annotation { "Feature Type Name" : "Feature", "Feature Type Description" : "" }
export const myFeature = defineFeature(function(context is Context, id is Id, definition is map)
    precondition{}
    {
        {
            var Q0;
            Q0=qCreatedBy(makeId("Top.planeOp"),FACE);
            var sketch = newSketch(context, id + "F0", { "sketchPlane" : qUnion([Q0])});
            skLineSegment(sketch, "E0.bottom", {"start": v(-50.8, 64.52) * mm, "end": v(89.2, 64.52) * mm});
            skLineSegment(sketch, "E0.top", {"start": v(-50.8, -85.48) * mm, "end": v(89.2, -85.48) * mm});
            skLineSegment(sketch, "E0.left", {"start": v(-50.8, 64.52) * mm, "end": v(-50.8, -85.48) * mm});
            skLineSegment(sketch, "E0.right", {"start": v(89.2, 64.52) * mm, "end": v(89.2, -85.48) * mm});
            skSolve(sketch);
        }
        {
            var Q0;
            Q0 = qSketchRegion(id + "F0", true);
            extrude(context, id + "F1", {"entities" : qUnion([Q0]), "depth" : 5 * mm, "offsetDistance" : 25 * mm});
        }
        {
            var Q0;
            Q0=makeQuery(id+"F1.opExtrude","CAP_FACE",FACE,{"disambiguationData":[OSD([sQuery(id+"F0.wireOp",EDGE,"E0.bottom"),sQuery(id+"F0.wireOp",EDGE,"E0.top"),sQuery(id+"F0.wireOp",EDGE,"E0.left"),sQuery(id+"F0.wireOp",EDGE,"E0.right")])],"isStart":false});
            var sketch = newSketch(context, id + "F2", { "sketchPlane" : qUnion([Q0])});
            skText(sketch, "E1", { "text": "UM2GO", "fontName": "OpenSans-Bold.ttf"});
            skText(sketch, "E2", { "text": "UM2+", "fontName": "OpenSans-Bold.ttf"});
            skText(sketch, "E3", { "text": "UM2+XTD", "fontName": "OpenSans-Bold.ttf"});
            skText(sketch, "E4", { "text": "UM3", "fontName": "OpenSans-Bold.ttf"});
            skText(sketch, "E5", { "text": "UM3XTD", "fontName": "OpenSans-Bold.ttf"});
            skText(sketch, "E6", { "text": "UM3XL", "fontName": "OpenSans-Bold.ttf"});
            skText(sketch, "E7", { "text": "KEEP CLEAR", "fontName": "OpenSans-Bold.ttf"});
            const initialGuessF2  = {"E1": [-0.0108, 0.0446, 1, 0, 0.014], "E2": [-0.0108, 0.0266, 1, 0, 0.014], "E3": [-0.0108, 0.0086, 1, 0, 0.014], "E4": [-0.0108, -0.0094, 1, 0, 0.014], "E5": [-0.0108, -0.0274, 1, 0, 0.014], "E6": [-0.0108, -0.0454, 1, 0, 0.014], "E7": [-0.0108, -0.0614, 1, 0, 0.012]};
            skSetInitialGuess(sketch, initialGuessF2);
            skSolve(sketch);
        }
        {
            var Q0;
            Q0 = qSketchRegion(id + "F2", true);
            extrude(context, id + "F3", {"entities" : qUnion([Q0]), "operationType" : NewBodyOperationType.REMOVE, "oppositeDirection" : true, "depth" : 2 * mm, "offsetDistance" : 25 * mm});
        }
        {
            var Q0;
            {var subQ0=sQuery(id+"F0.wireOp",EDGE,"E0.left");var subQ1=sQuery(id+"F0.wireOp",EDGE,"E0.top");var subQ2=sQuery(id+"F0.wireOp",EDGE,"E0.bottom");var subQ3=sQuery(id+"F0.wireOp",EDGE,"E0.right");Q0=makeQuery(id+"F3.boolean.opBoolean","SPLIT",FACE,{"disambiguationData":[TD([makeQuery(id+"F1.opExtrude","SWEPT_FACE",FACE,{"disambiguationData":[OSD([subQ2])]})])],"derivedFrom":makeQuery(id+"F1.opExtrude","CAP_FACE",FACE,{"disambiguationData":[OSD([subQ2,subQ1,subQ0,subQ3])],"isStart":false})});}
            var sketch = newSketch(context, id + "F4", { "sketchPlane" : qUnion([Q0])});
            skLineSegment(sketch, "E8.bottom", {"start": v(-36.8, 52.56) * mm, "end": v(-26.3, 52.56) * mm});
            skLineSegment(sketch, "E8.top", {"start": v(-36.8, 50.06) * mm, "end": v(-26.3, 50.06) * mm});
            skLineSegment(sketch, "E8.left", {"start": v(-36.8, 52.56) * mm, "end": v(-36.8, 50.06) * mm});
            skLineSegment(sketch, "E8.right", {"start": v(-26.3, 52.56) * mm, "end": v(-26.3, 50.06) * mm});
            skLineSegment(sketch, "E9.bottom", {"start": v(-36.8, 35.06) * mm, "end": v(-26.3, 35.06) * mm});
            skLineSegment(sketch, "E9.top", {"start": v(-36.8, 32.56) * mm, "end": v(-26.3, 32.56) * mm});
            skLineSegment(sketch, "E9.left", {"start": v(-36.8, 35.06) * mm, "end": v(-36.8, 32.56) * mm});
            skLineSegment(sketch, "E9.right", {"start": v(-26.3, 35.06) * mm, "end": v(-26.3, 32.56) * mm});
            skLineSegment(sketch, "E10.bottom", {"start": v(-36.8, 17.56) * mm, "end": v(-26.3, 17.56) * mm});
            skLineSegment(sketch, "E10.top", {"start": v(-36.8, 15.06) * mm, "end": v(-26.3, 15.06) * mm});
            skLineSegment(sketch, "E10.left", {"start": v(-36.8, 17.56) * mm, "end": v(-36.8, 15.06) * mm});
            skLineSegment(sketch, "E10.right", {"start": v(-26.3, 17.56) * mm, "end": v(-26.3, 15.06) * mm});
            skLineSegment(sketch, "E11.bottom", {"start": v(-36.8, 0.06) * mm, "end": v(-26.3, 0.06) * mm});
            skLineSegment(sketch, "E11.top", {"start": v(-36.8, -2.44) * mm, "end": v(-26.3, -2.44) * mm});
            skLineSegment(sketch, "E11.left", {"start": v(-36.8, 0.06) * mm, "end": v(-36.8, -2.44) * mm});
            skLineSegment(sketch, "E11.right", {"start": v(-26.3, 0.06) * mm, "end": v(-26.3, -2.44) * mm});
            skLineSegment(sketch, "E12.bottom", {"start": v(-36.8, -17.44) * mm, "end": v(-26.3, -17.44) * mm});
            skLineSegment(sketch, "E12.top", {"start": v(-36.8, -19.94) * mm, "end": v(-26.3, -19.94) * mm});
            skLineSegment(sketch, "E12.left", {"start": v(-36.8, -17.44) * mm, "end": v(-36.8, -19.94) * mm});
            skLineSegment(sketch, "E12.right", {"start": v(-26.3, -17.44) * mm, "end": v(-26.3, -19.94) * mm});
            skLineSegment(sketch, "E13.bottom", {"start": v(-36.8, -34.94) * mm, "end": v(-26.3, -34.94) * mm});
            skLineSegment(sketch, "E13.top", {"start": v(-36.8, -37.44) * mm, "end": v(-26.3, -37.44) * mm});
            skLineSegment(sketch, "E13.left", {"start": v(-36.8, -34.94) * mm, "end": v(-36.8, -37.44) * mm});
            skLineSegment(sketch, "E13.right", {"start": v(-26.3, -34.94) * mm, "end": v(-26.3, -37.44) * mm});
            skLineSegment(sketch, "E14.bottom", {"start": v(-36.8, -52.44) * mm, "end": v(-26.3, -52.44) * mm});
            skLineSegment(sketch, "E14.top", {"start": v(-36.8, -54.94) * mm, "end": v(-26.3, -54.94) * mm});
            skLineSegment(sketch, "E14.left", {"start": v(-36.8, -52.44) * mm, "end": v(-36.8, -54.94) * mm});
            skLineSegment(sketch, "E14.right", {"start": v(-26.3, -52.44) * mm, "end": v(-26.3, -54.94) * mm});
            skLineSegment(sketch, "E15.bottom", {"start": v(75.2, -79.48) * mm, "end": v(85.2, -79.48) * mm});
            skLineSegment(sketch, "E15.top", {"start": v(75.2, -81.48) * mm, "end": v(85.2, -81.48) * mm});
            skLineSegment(sketch, "E15.left", {"start": v(75.2, -79.48) * mm, "end": v(75.2, -81.48) * mm});
            skLineSegment(sketch, "E15.right", {"start": v(85.2, -79.48) * mm, "end": v(85.2, -81.48) * mm});
            skLineSegment(sketch, "E16.bottom", {"start": v(-46.8, 60.52) * mm, "end": v(-36.8, 60.52) * mm});
            skLineSegment(sketch, "E16.top", {"start": v(-46.8, 58.52) * mm, "end": v(-36.8, 58.52) * mm});
            skLineSegment(sketch, "E16.left", {"start": v(-46.8, 60.52) * mm, "end": v(-46.8, 58.52) * mm});
            skLineSegment(sketch, "E16.right", {"start": v(-36.8, 60.52) * mm, "end": v(-36.8, 58.52) * mm});
            skLineSegment(sketch, "E17.bottom", {"start": v(-46.8, -79.48) * mm, "end": v(-36.8, -79.48) * mm});
            skLineSegment(sketch, "E17.top", {"start": v(-46.8, -81.48) * mm, "end": v(-36.8, -81.48) * mm});
            skLineSegment(sketch, "E17.left", {"start": v(-46.8, -79.48) * mm, "end": v(-46.8, -81.48) * mm});
            skLineSegment(sketch, "E17.right", {"start": v(-36.8, -79.48) * mm, "end": v(-36.8, -81.48) * mm});
            skLineSegment(sketch, "E18.bottom", {"start": v(-66.51, -95.44) * mm, "end": v(-56.51, -95.44) * mm});
            skLineSegment(sketch, "E18.top", {"start": v(-66.51, -97.44) * mm, "end": v(-56.51, -97.44) * mm});
            skLineSegment(sketch, "E18.left", {"start": v(-66.51, -95.44) * mm, "end": v(-66.51, -97.44) * mm});
            skLineSegment(sketch, "E18.right", {"start": v(-56.51, -95.44) * mm, "end": v(-56.51, -97.44) * mm});
            skLineSegment(sketch, "E19.bottom", {"start": v(-37.13, -117.06) * mm, "end": v(-27.13, -117.06) * mm});
            skLineSegment(sketch, "E19.top", {"start": v(-37.13, -119.06) * mm, "end": v(-27.13, -119.06) * mm});
            skLineSegment(sketch, "E19.left", {"start": v(-37.13, -117.06) * mm, "end": v(-37.13, -119.06) * mm});
            skLineSegment(sketch, "E19.right", {"start": v(-27.13, -117.06) * mm, "end": v(-27.13, -119.06) * mm});
            skLineSegment(sketch, "E20.bottom", {"start": v(11.28, -116.94) * mm, "end": v(21.28, -116.94) * mm});
            skLineSegment(sketch, "E20.top", {"start": v(11.28, -118.94) * mm, "end": v(21.28, -118.94) * mm});
            skLineSegment(sketch, "E20.left", {"start": v(11.28, -116.94) * mm, "end": v(11.28, -118.94) * mm});
            skLineSegment(sketch, "E20.right", {"start": v(21.28, -116.94) * mm, "end": v(21.28, -118.94) * mm});
            skLineSegment(sketch, "E21.bottom", {"start": v(75.2, 60.52) * mm, "end": v(85.2, 60.52) * mm});
            skLineSegment(sketch, "E21.top", {"start": v(75.2, 58.52) * mm, "end": v(85.2, 58.52) * mm});
            skLineSegment(sketch, "E21.left", {"start": v(75.2, 60.52) * mm, "end": v(75.2, 58.52) * mm});
            skLineSegment(sketch, "E21.right", {"start": v(85.2, 60.52) * mm, "end": v(85.2, 58.52) * mm});
            skLineSegment(sketch, "E22.bottom", {"start": v(-46.73, 201.68) * mm, "end": v(-36.73, 201.68) * mm});
            skLineSegment(sketch, "E22.top", {"start": v(-46.73, 199.68) * mm, "end": v(-36.73, 199.68) * mm});
            skLineSegment(sketch, "E22.left", {"start": v(-46.73, 201.68) * mm, "end": v(-46.73, 199.68) * mm});
            skLineSegment(sketch, "E22.right", {"start": v(-36.73, 201.68) * mm, "end": v(-36.73, 199.68) * mm});
            skSolve(sketch);
        }
        {
            var Q0;
            Q0 = qSketchRegion(id + "F4", true);
            extrude(context, id + "F5", {"entities" : qUnion([Q0]), "operationType" : NewBodyOperationType.REMOVE, "oppositeDirection" : true, "depth" : 25 * mm, "offsetDistance" : 25 * mm});
        }
    });